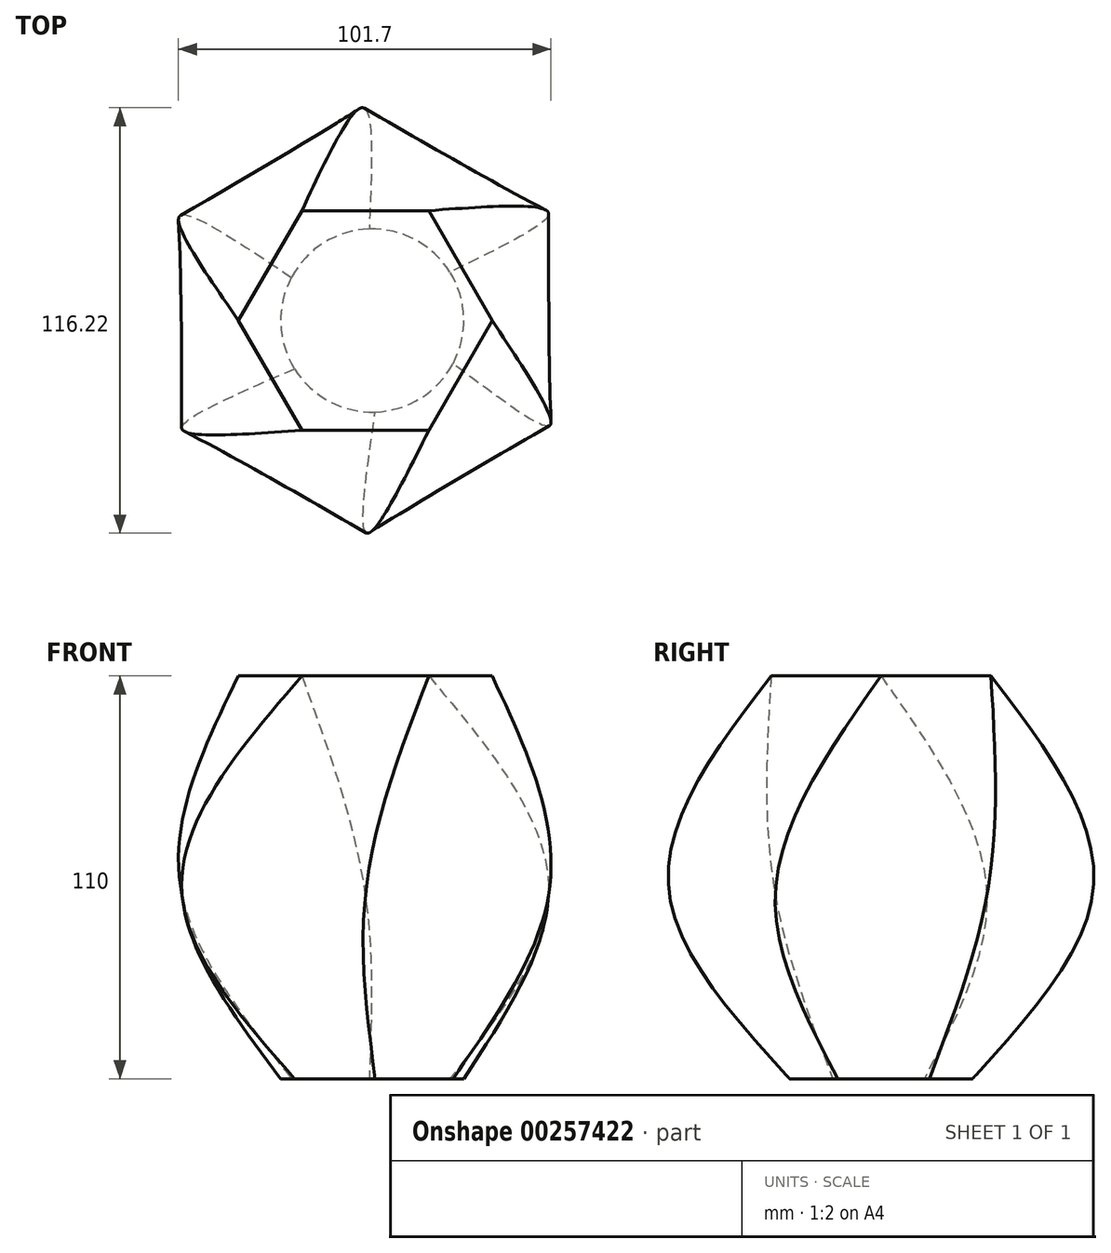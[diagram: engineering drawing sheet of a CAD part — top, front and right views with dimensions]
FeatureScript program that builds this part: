
annotation { "Feature Type Name" : "Feature", "Feature Type Description" : "" }
export const myFeature = defineFeature(function(context is Context, id is Id, definition is map)
    precondition{}
    {
        {
            var Q0;
            Q0=qCreatedBy(makeId("Top.planeOp"),FACE);
            var sketch = newSketch(context, id + "F0", { "sketchPlane" : qUnion([Q0])});
            skCircle(sketch, "E0.cCircle", {"center": v(0, 0) * mm, "radius": 30 * mm, "construction": true});
            skLineSegment(sketch, "E0.0", {"start": v(-17.32, 30) * mm, "end": v(17.32, 30) * mm});
            skLineSegment(sketch, "E0.1", {"start": v(17.32, 30) * mm, "end": v(34.64, 0) * mm});
            skLineSegment(sketch, "E0.2", {"start": v(34.64, 0) * mm, "end": v(17.32, -30) * mm});
            skLineSegment(sketch, "E0.3", {"start": v(17.32, -30) * mm, "end": v(-17.32, -30) * mm});
            skLineSegment(sketch, "E0.4", {"start": v(-17.32, -30) * mm, "end": v(-34.64, 0) * mm});
            skLineSegment(sketch, "E0.5", {"start": v(-34.64, 0) * mm, "end": v(-17.32, 30) * mm});
            skPoint(sketch, "E0.0.midPoint", {"position": v(0, 30) * mm});
            skSolve(sketch);
        }
        {
            var Q0;
            Q0=qCreatedBy(makeId("Top.planeOp"),FACE);
            cPlane(context, id + "F1", {"entities" : qUnion([Q0]), "cplaneType" : CPlaneType.OFFSET, "offset" : 60 * mm, "oppositeDirection" : true, "width" : 150 * mm, "height" : 150 * mm});
        }
        {
            var Q0;
            Q0=qCreatedBy(id+"F1.planeOp",FACE);
            var sketch = newSketch(context, id + "F2", { "sketchPlane" : qUnion([Q0])});
            skCircle(sketch, "E1.cCircle", {"center": v(0, 0) * mm, "radius": 50 * mm, "construction": true});
            skLineSegment(sketch, "E1.0", {"start": v(0, 57.74) * mm, "end": v(50, 28.87) * mm});
            skLineSegment(sketch, "E1.1", {"start": v(50, 28.87) * mm, "end": v(50, -28.87) * mm});
            skLineSegment(sketch, "E1.2", {"start": v(50, -28.87) * mm, "end": v(0, -57.74) * mm});
            skLineSegment(sketch, "E1.3", {"start": v(0, -57.74) * mm, "end": v(-50, -28.87) * mm});
            skLineSegment(sketch, "E1.4", {"start": v(-50, -28.87) * mm, "end": v(-50, 28.87) * mm});
            skLineSegment(sketch, "E1.5", {"start": v(-50, 28.87) * mm, "end": v(0, 57.74) * mm});
            skPoint(sketch, "E1.0.midPoint", {"position": v(25, 43.3) * mm});
            skSolve(sketch);
        }
        {
            var Q0;
            Q0=qCreatedBy(id+"F1.planeOp",FACE);
            cPlane(context, id + "F3", {"entities" : qUnion([Q0]), "cplaneType" : CPlaneType.OFFSET, "offset" : 50 * mm, "oppositeDirection" : true, "width" : 150 * mm, "height" : 150 * mm});
        }
        {
            var Q0;
            Q0=qCreatedBy(id+"F3.planeOp",FACE);
            var sketch = newSketch(context, id + "F4", { "sketchPlane" : qUnion([Q0])});
            skCircle(sketch, "E2", {"center": v(1.9, 0) * mm, "radius": 25 * mm});
            skSolve(sketch);
        }
        {
            var Q0;
            Q0=makeQuery(id+"F0.imprint","IMPRINT",FACE,{"disambiguationData":[TD([[makeQuery(id+"F0.imprint","IMPRINT",EDGE,{"derivedFrom":sQuery(id+"F0.wireOp",EDGE,"E0.0")}),-1.0]])]});
            var Q1;
            Q1=makeQuery(id+"F2.imprint","IMPRINT",FACE,{"disambiguationData":[TD([[makeQuery(id+"F2.imprint","IMPRINT",EDGE,{"derivedFrom":sQuery(id+"F2.wireOp",EDGE,"E1.0")}),-1.0]])]});
            var Q2;
            Q2=makeQuery(id+"F4.imprint","IMPRINT",FACE,{"disambiguationData":[TD([[makeQuery(id+"F4.imprint","IMPRINT",EDGE,{"derivedFrom":sQuery(id+"F4.wireOp",EDGE,"E2")}),1.0]])]});
            loft(context, id + "F5", {"sheetProfilesArray" : [{ "sheetProfileEntities" : qUnion([Q0]) }, { "sheetProfileEntities" : qUnion([Q1]) }, { "sheetProfileEntities" : qUnion([Q2]) }]});
        }
    });
